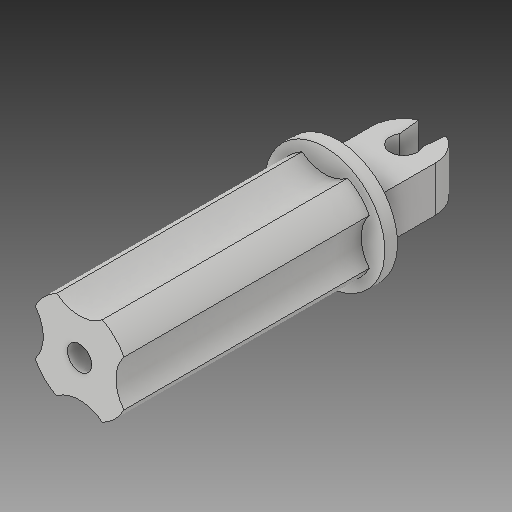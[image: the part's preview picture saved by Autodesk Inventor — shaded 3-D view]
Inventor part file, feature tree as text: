
AUTODESK INVENTOR PART (.ipt)
format: ipt  version: 2019 (Build 230136000, 136)  size: 160,768 bytes
history: native  units: in
note: dims shown in document units (in); Inventor stores cm internally (conversion verified against a paired STEP export)
features: sketch x6, other x3
ambient origin geometry x8: Origin, YZ Plane, XZ Plane, XY Plane, X Axis, Y Axis, Z Axis, Center Point
bodies: Solid1 (feature_tree)
feature tree (9):
  other  "Top.ipt"
  other  "Solid1::Top.ipt"
  other  "TaggingFeature1"
  sketch  "Sketch1"  dims[d0=0.3937in]
  sketch  "Sketch2"
  sketch  "Sketch3"
  sketch  "Sketch4"
  sketch  "Sketch5"
  sketch  "Sketch6"
